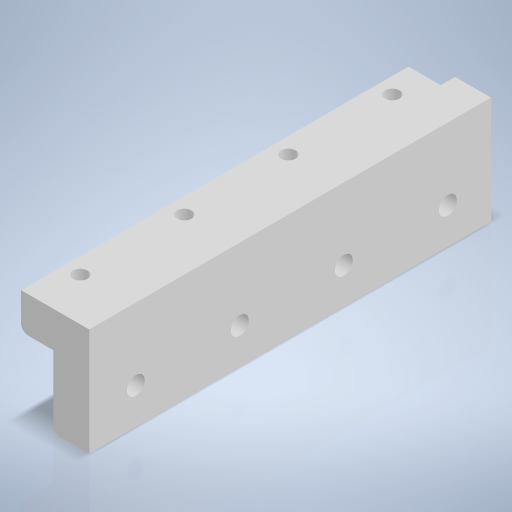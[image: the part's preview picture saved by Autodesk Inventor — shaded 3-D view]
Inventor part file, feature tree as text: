
AUTODESK INVENTOR PART (.ipt)
format: ipt  version: 2024 (Build 280153000, 153)  size: 251,904 bytes
history: native  units: mm
features: sketch x4, extrude x2, hole x2, fillet x1
ambient origin geometry x8: Origin, YZ Plane, XZ Plane, XY Plane, X Axis, Y Axis, Z Axis, Center Point
bodies: Volumenkörper1 (feature_tree)
feature tree (9):
  extrude  "Extrusion1"  Depth=20.0mm
  hole  "Bohrung1"  [1 undecoded]
  hole  "Bohrung2"  [1 undecoded]
  extrude  "Extrusion2"  Depth=4.0mm
  fillet  "Rundung1"  Radius=29.0mm
  sketch  "Skizze2"  dims[d6=10.0mm d7=20.0mm]
  sketch  "Skizze3"  dims[d8=10.0mm d9=9.0mm]
  sketch  "Skizze4"  dims[d10=112.0mm d11=0.0mm d12=13.0mm]
  sketch  "Skizze5"  dims[d13=29.0mm d14=29.0mm d15=29.0mm d16=4.0mm d17=12.0mm d18=5.0mm d19=2.0mm d20=90.0deg d21=8.0mm d22=0.0mm d23=5.0mm d24=6.0mm d25=4.0mm d26=2.0mm d27=90.0deg d28=8.0mm d29=0.0mm d30=12.0mm d31=29.0mm d32=29.0mm d33=29.0mm d36=112.0mm d37=0.0mm d38=2.0mm d40=4.0mm]
note: 2 required parameter values undecoded (feature->parameter linkage not recoverable at this tier; creation-order binding heuristic only, values carry confidence <= 0.55)
